# Revit family: Faucet-Kitchen_Sink-KOHLER-Coralais-K-15171
name_source: partatom
category: Plumbing Fixtures
revit_build: Autodesk Revit 2015 (Build: 20140606_1530(x64)
units: mm (PartAtom-declared; Revit-internal decimal feet)

## types (3) — shared parameters
ADA Compliant = Yes
Assembly Code = D2010900
CW Connection = Yes
Date Modified = 09/12/2017
Default Elevation = 36"
Description = Coralais Three-hole kitchen sink faucet with 8-1/2inch spout, ground joints and lever handle
Flow Rate = 2 GPM
HW Connection = Yes
Height = 7 11/16"
Inlet Connector = Inlet Connection
Length = 10 1/2"
Manufacturer = KOHLER Co.
MasterFormat 1995 = 15410
MasterFormat 2004 = 22.41.39
Material = Metal Construction
Outlet Connector = Outlet Connection
Pressure = 60.00 psi
Product Documentation Link = http://www.us.kohler.com
Product Name = Coralais
Product Page URL = http://www.us.kohler.com
Spout Reach = 8 1/2"
URL = http://www.us.kohler.com
Waste Connection = Yes
Width = 10 1/4"

## per-type parameters (varying)
| type | Finish | Model | Type |
| CP-Polished Chrome | Kohler-Metal-CP-Polished_Chrome | K-15171-F-CP | 1 |
| G-Brushed Chrome | Kohler-Metal-G-Brushed_Chrome | K-15171-F-G | 2 |
| BN-Vibrant Brushed Nickel | Kohler-Metal-BN-Vibrant_Brushed_Nickel | K-15171-F-BN | 3 |

## geometry (parser evidence)
native form markers: Blend x2, Sweep x6
no freeform markers — native parametric forms only
